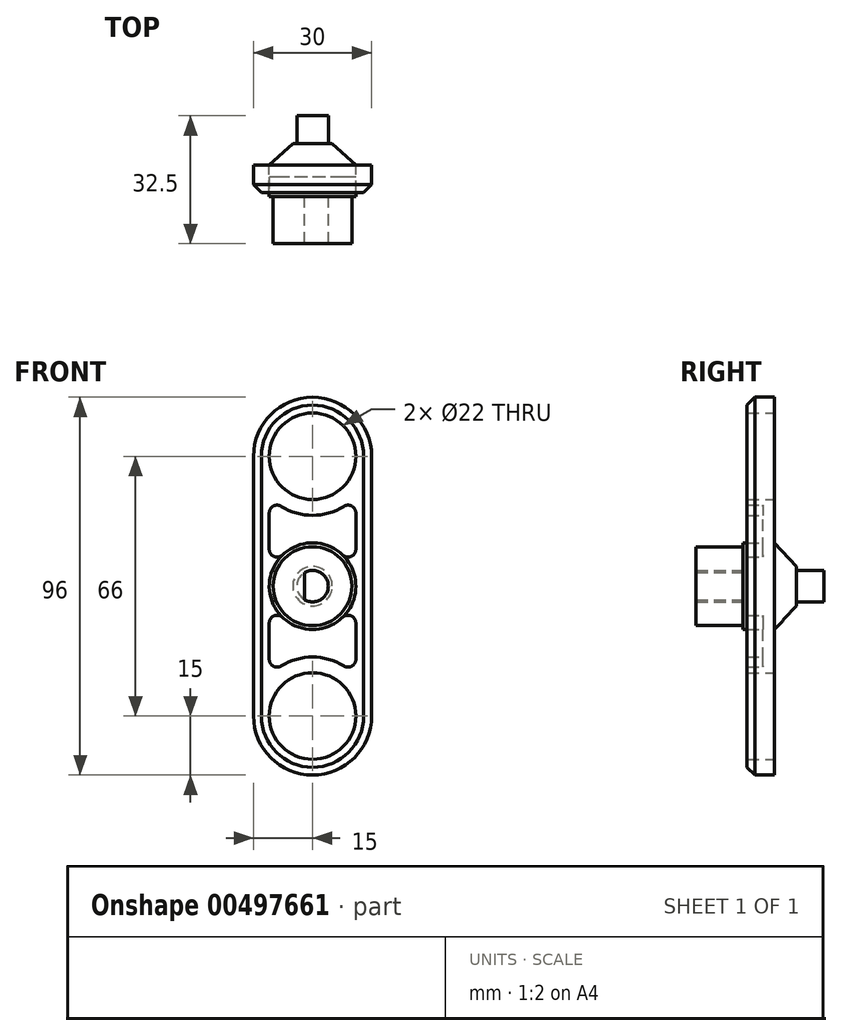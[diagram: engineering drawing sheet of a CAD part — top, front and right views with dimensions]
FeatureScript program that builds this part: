
annotation { "Feature Type Name" : "Feature", "Feature Type Description" : "" }
export const myFeature = defineFeature(function(context is Context, id is Id, definition is map)
    precondition{}
    {
        {
            var Q0;
            Q0=qCreatedBy(makeId("Front.planeOp"),FACE);
            var sketch = newSketch(context, id + "F0", { "sketchPlane" : qUnion([Q0])});
            skCircle(sketch, "E0", {"center": v(0, 0) * mm, "radius": 4 * mm});
            skCircle(sketch, "E1", {"center": v(0, 33) * mm, "radius": 4 * mm});
            skCircle(sketch, "E2", {"center": v(0, -33) * mm, "radius": 4 * mm});
            skCircle(sketch, "E3", {"center": v(0, 33) * mm, "radius": 15 * mm});
            skCircle(sketch, "E4", {"center": v(0, -33) * mm, "radius": 15 * mm});
            skLineSegment(sketch, "E5", {"start": v(-15, -33) * mm, "end": v(-15, 33) * mm});
            skLineSegment(sketch, "E6", {"start": v(15, -33) * mm, "end": v(15, 33) * mm});
            skCircle(sketch, "E7", {"center": v(0, 33) * mm, "radius": 11 * mm});
            skCircle(sketch, "E8", {"center": v(0, -33) * mm, "radius": 11 * mm});
            skArc(sketch, "E9", {"start": v(8.26, 5.64) * mm, "mid": v(0, 10) * mm, "end": v(-8.26, 5.64) * mm});
            skLineSegment(sketch, "E10", {"start": v(-11, -22.8) * mm, "end": v(-11, -9.38) * mm});
            skLineSegment(sketch, "E11", {"start": v(11, -22.8) * mm, "end": v(11, -9.38) * mm});
            skLineSegment(sketch, "E12", {"start": v(-11, 9.38) * mm, "end": v(-11, 22.8) * mm});
            skLineSegment(sketch, "E13", {"start": v(11, 9.38) * mm, "end": v(11, 22.8) * mm});
            skArc(sketch, "E14.MirrorCS", {"start": v(8.26, -5.64) * mm, "mid": v(0, -10) * mm, "end": v(-8.26, -5.64) * mm});
            skPoint(sketch, "E15.visualSharp", {"position": v(-10, 0) * mm});
            skArc(sketch, "E15.filletArc", {"start": v(-11, 9.38) * mm, "mid": v(-9.78, 7.54) * mm, "end": v(-7.62, 7.94) * mm});
            skArc(sketch, "E16.filletArc", {"start": v(-7.62, -7.94) * mm, "mid": v(-9.78, -7.54) * mm, "end": v(-11, -9.38) * mm});
            skPoint(sketch, "E17.visualSharp", {"position": v(10, 0) * mm});
            skArc(sketch, "E17.filletArc", {"start": v(11, -9.38) * mm, "mid": v(9.78, -7.54) * mm, "end": v(7.62, -7.94) * mm});
            skArc(sketch, "E18.filletArc", {"start": v(7.62, 7.94) * mm, "mid": v(9.78, 7.54) * mm, "end": v(11, 9.38) * mm});
            skLineSegment(sketch, "E19", {"start": v(-2, -3.46) * mm, "end": v(-2, 3.46) * mm});
            skArc(sketch, "E20", {"start": v(8.26, -5.64) * mm, "mid": v(10, 0) * mm, "end": v(8.26, 5.64) * mm});
            skArc(sketch, "E21", {"start": v(-8.26, 5.64) * mm, "mid": v(-10, 0) * mm, "end": v(-8.26, -5.64) * mm});
            skCircle(sketch, "E22", {"center": v(0, 0) * mm, "radius": 11 * mm});
            skSolve(sketch);
        }
        {
            var Q0;
            Q0=makeQuery(id+"F0.imprint","IMPRINT",FACE,{"disambiguationData":[TD([[makeQuery(id+"F0.imprint","IMPRINT",EDGE,{"derivedFrom":sQuery(id+"F0.wireOp",EDGE,"E7")}),-1.0]])]});
            var Q1;
            Q1=makeQuery(id+"F0.imprint","IMPRINT",FACE,{"disambiguationData":[TD([[makeQuery(id+"F0.imprint","IMPRINT",EDGE,{"derivedFrom":sQuery(id+"F0.wireOp",EDGE,"E8")}),-1.0]])]});
            var Q2;
            {var subQ1=sQuery(id+"F0.wireOp",EDGE,"E5");Q2=makeQuery(id+"F0.imprint","IMPRINT",FACE,{"disambiguationData":[TD([[makeQuery(id+"F0.imprint","IMPRINT",EDGE,{"derivedFrom":subQ1}),-1.0]])]});}
            var Q3;
            {var subQ0=sQuery(id+"F0.wireOp",EDGE,"E6");Q3=makeQuery(id+"F0.imprint","IMPRINT",FACE,{"disambiguationData":[TD([[makeQuery(id+"F0.imprint","IMPRINT",EDGE,{"derivedFrom":subQ0}),1.0]])]});}
            var Q4;
            {var subQ0=sQuery(id+"F0.wireOp",EDGE,"E21");Q4=makeQuery(id+"F0.imprint","IMPRINT",FACE,{"disambiguationData":[TD([[makeQuery(id+"F0.imprint","IMPRINT",EDGE,{"derivedFrom":subQ0}),-1.0]])]});}
            var Q5;
            {var subQ0=sQuery(id+"F0.wireOp",EDGE,"E20");Q5=makeQuery(id+"F0.imprint","IMPRINT",FACE,{"disambiguationData":[TD([[makeQuery(id+"F0.imprint","IMPRINT",EDGE,{"derivedFrom":subQ0}),-1.0]])]});}
            var Q6;
            Q6=makeQuery(id+"F0.imprint","IMPRINT",FACE,{"disambiguationData":[TD([[makeQuery(id+"F0.imprint","IMPRINT",EDGE,{"derivedFrom":sQuery(id+"F0.wireOp",EDGE,"E9")}),1.0]])]});
            var Q7;
            {var subQ0=sQuery(id+"F0.wireOp",EDGE,"E19");Q7=makeQuery(id+"F0.imprint","IMPRINT",FACE,{"disambiguationData":[TD([[makeQuery(id+"F0.imprint","IMPRINT",EDGE,{"derivedFrom":subQ0}),1.0]])]});}
            var Q8;
            {var subQ0=sQuery(id+"F0.wireOp",EDGE,"E19");Q8=makeQuery(id+"F0.imprint","IMPRINT",FACE,{"disambiguationData":[TD([[makeQuery(id+"F0.imprint","IMPRINT",EDGE,{"derivedFrom":subQ0}),-1.0]])]});}
            extrude(context, id + "F1", {"entities" : qUnion([Q0, Q1, Q2, Q3, Q4, Q5, Q6, Q7, Q8]), "depth" : 7 * mm});
        }
        {
            var Q0;
            Q0=makeQuery(id+"F0.imprint","IMPRINT",FACE,{"disambiguationData":[TD([[makeQuery(id+"F0.imprint","IMPRINT",EDGE,{"derivedFrom":sQuery(id+"F0.wireOp",EDGE,"E0")}),-1.0]])]});
            var Q1;
            {var subQ0=sQuery(id+"F0.wireOp",EDGE,"E19");Q1=makeQuery(id+"F0.imprint","IMPRINT",FACE,{"disambiguationData":[TD([[makeQuery(id+"F0.imprint","IMPRINT",EDGE,{"derivedFrom":subQ0}),1.0]])]});}
            extrude(context, id + "F2", {"entities" : qUnion([Q0, Q1]), "operationType" : NewBodyOperationType.ADD, "depth" : 20 * mm});
        }
        {
            var Q0;
            Q0=makeQuery(id+"F0.imprint","IMPRINT",FACE,{"disambiguationData":[TD([[makeQuery(id+"F0.imprint","IMPRINT",EDGE,{"derivedFrom":sQuery(id+"F0.wireOp",EDGE,"E0")}),1.0]])]});
            extrude(context, id + "F3", {"entities" : qUnion([Q0]), "operationType" : NewBodyOperationType.ADD, "depth" : 3 * mm, "hasSecondDirection" : true, "secondDirectionOppositeDirection" : true, "secondDirectionDepth" : 12.5 * mm});
        }
        {
            var Q0;
            {var subQ2=sQuery(id+"F0.wireOp",EDGE,"E12");Q0=makeQuery(id+"F0.imprint","IMPRINT",FACE,{"disambiguationData":[TD([[makeQuery(id+"F0.imprint","IMPRINT",EDGE,{"derivedFrom":subQ2}),-1.0]])]});}
            var Q1;
            {var subQ2=sQuery(id+"F0.wireOp",EDGE,"E10");Q1=makeQuery(id+"F0.imprint","IMPRINT",FACE,{"disambiguationData":[TD([[makeQuery(id+"F0.imprint","IMPRINT",EDGE,{"derivedFrom":subQ2}),-1.0]])]});}
            var Q2;
            {var subQ0=sQuery(id+"F0.wireOp",EDGE,"E9");Q2=makeQuery(id+"F0.imprint","IMPRINT",FACE,{"disambiguationData":[TD([[makeQuery(id+"F0.imprint","IMPRINT",EDGE,{"derivedFrom":subQ0}),-1.0]])]});}
            var Q3;
            {var subQ0=sQuery(id+"F0.wireOp",EDGE,"E14.MirrorCS");Q3=makeQuery(id+"F0.imprint","IMPRINT",FACE,{"disambiguationData":[TD([[makeQuery(id+"F0.imprint","IMPRINT",EDGE,{"derivedFrom":subQ0}),1.0]])]});}
            extrude(context, id + "F4", {"entities" : qUnion([Q0, Q1, Q2, Q3]), "operationType" : NewBodyOperationType.ADD, "depth" : 3 * mm});
        }
        {
            var Q0;
            Q0=makeQuery(id+"F1.opExtrude","SWEPT_EDGE",EDGE,{"disambiguationData":[OSD([sQuery(id+"F0.wireOp",EDGE,"E4"),sQuery(id+"F0.wireOp",EDGE,"E10")])]});
            var Q1;
            Q1=makeQuery(id+"F1.opExtrude","SWEPT_EDGE",EDGE,{"disambiguationData":[OSD([sQuery(id+"F0.wireOp",EDGE,"E4"),sQuery(id+"F0.wireOp",EDGE,"E11")])]});
            var Q2;
            Q2=makeQuery(id+"F1.opExtrude","SWEPT_EDGE",EDGE,{"disambiguationData":[OSD([sQuery(id+"F0.wireOp",EDGE,"E3"),sQuery(id+"F0.wireOp",EDGE,"E13")])]});
            var Q3;
            Q3=makeQuery(id+"F1.opExtrude","SWEPT_EDGE",EDGE,{"disambiguationData":[OSD([sQuery(id+"F0.wireOp",EDGE,"E3"),sQuery(id+"F0.wireOp",EDGE,"E12")])]});
            fillet(context, id + "F5", {"entities" : qUnion([Q0, Q1, Q2, Q3]), "radius" : 2 * mm, "tangentPropagation" : true, "allowEdgeOverflow" : false});
        }
        {
            var Q0;
            {var subQ0=sQuery(id+"F0.wireOp",EDGE,"E14.MirrorCS");Q0=makeQuery(id+"F0.imprint","IMPRINT",FACE,{"disambiguationData":[TD([[makeQuery(id+"F0.imprint","IMPRINT",EDGE,{"derivedFrom":subQ0}),1.0]])]});}
            var Q1;
            {var subQ0=sQuery(id+"F0.wireOp",EDGE,"E20");Q1=makeQuery(id+"F0.imprint","IMPRINT",FACE,{"disambiguationData":[TD([[makeQuery(id+"F0.imprint","IMPRINT",EDGE,{"derivedFrom":subQ0}),-1.0]])]});}
            var Q2;
            {var subQ0=sQuery(id+"F0.wireOp",EDGE,"E21");Q2=makeQuery(id+"F0.imprint","IMPRINT",FACE,{"disambiguationData":[TD([[makeQuery(id+"F0.imprint","IMPRINT",EDGE,{"derivedFrom":subQ0}),-1.0]])]});}
            var Q3;
            {var subQ0=sQuery(id+"F0.wireOp",EDGE,"E9");Q3=makeQuery(id+"F0.imprint","IMPRINT",FACE,{"disambiguationData":[TD([[makeQuery(id+"F0.imprint","IMPRINT",EDGE,{"derivedFrom":subQ0}),-1.0]])]});}
            var Q4;
            Q4=makeQuery(id+"F0.imprint","IMPRINT",FACE,{"disambiguationData":[TD([[makeQuery(id+"F0.imprint","IMPRINT",EDGE,{"derivedFrom":sQuery(id+"F0.wireOp",EDGE,"E9")}),1.0]])]});
            extrude(context, id + "F6", {"entities" : qUnion([Q0, Q1, Q2, Q3, Q4]), "operationType" : NewBodyOperationType.ADD, "oppositeDirection" : true, "depth" : 5.5 * mm});
        }
        {
            var Q0;
            Q0=makeQuery(id+"F6.opExtrude","CAP_EDGE",EDGE,{"disambiguationData":[OSD([sQuery(id+"F0.wireOp",EDGE,"E22")])],"isStart":false});
            chamfer(context, id + "F7", {"entities" : qUnion([Q0]), "chamferType" : ChamferType.TWO_OFFSETS, "width1" : 5.5 * mm, "oppositeDirection" : false, "width2" : 6 * mm, "tangentPropagation" : true});
        }
        {
            var Q0;
            Q0=makeQuery(id+"F0.imprint","IMPRINT",FACE,{"disambiguationData":[TD([[makeQuery(id+"F0.imprint","IMPRINT",EDGE,{"derivedFrom":sQuery(id+"F0.wireOp",EDGE,"E9")}),-1.0]])]});
            extrude(context, id + "F8", {"entities" : qUnion([Q0]), "operationType" : NewBodyOperationType.ADD, "depth" : (7 + 1) * mm});
        }
        {
            var Q0;
            {var subQ0=sQuery(id+"F0.wireOp",EDGE,"E3");Q0=makeQuery(id+"F1.opExtrude","CAP_EDGE",EDGE,{"disambiguationData":[OSD([subQ0]),TDD([makeQuery(id+"F0.imprint","IMPRINT",EDGE,{"disambiguationData":[TD([[makeQuery(id+"F0.imprint","INTERSECT",VERTEX,{"derivedFrom":[subQ0,sQuery(id+"F0.wireOp",EDGE,"E5")]}),1.0]])],"derivedFrom":subQ0})])],"isStart":false});}
            chamfer(context, id + "F9", {"entities" : qUnion([Q0]), "width" : 2 * mm, "tangentPropagation" : true});
        }
    });
